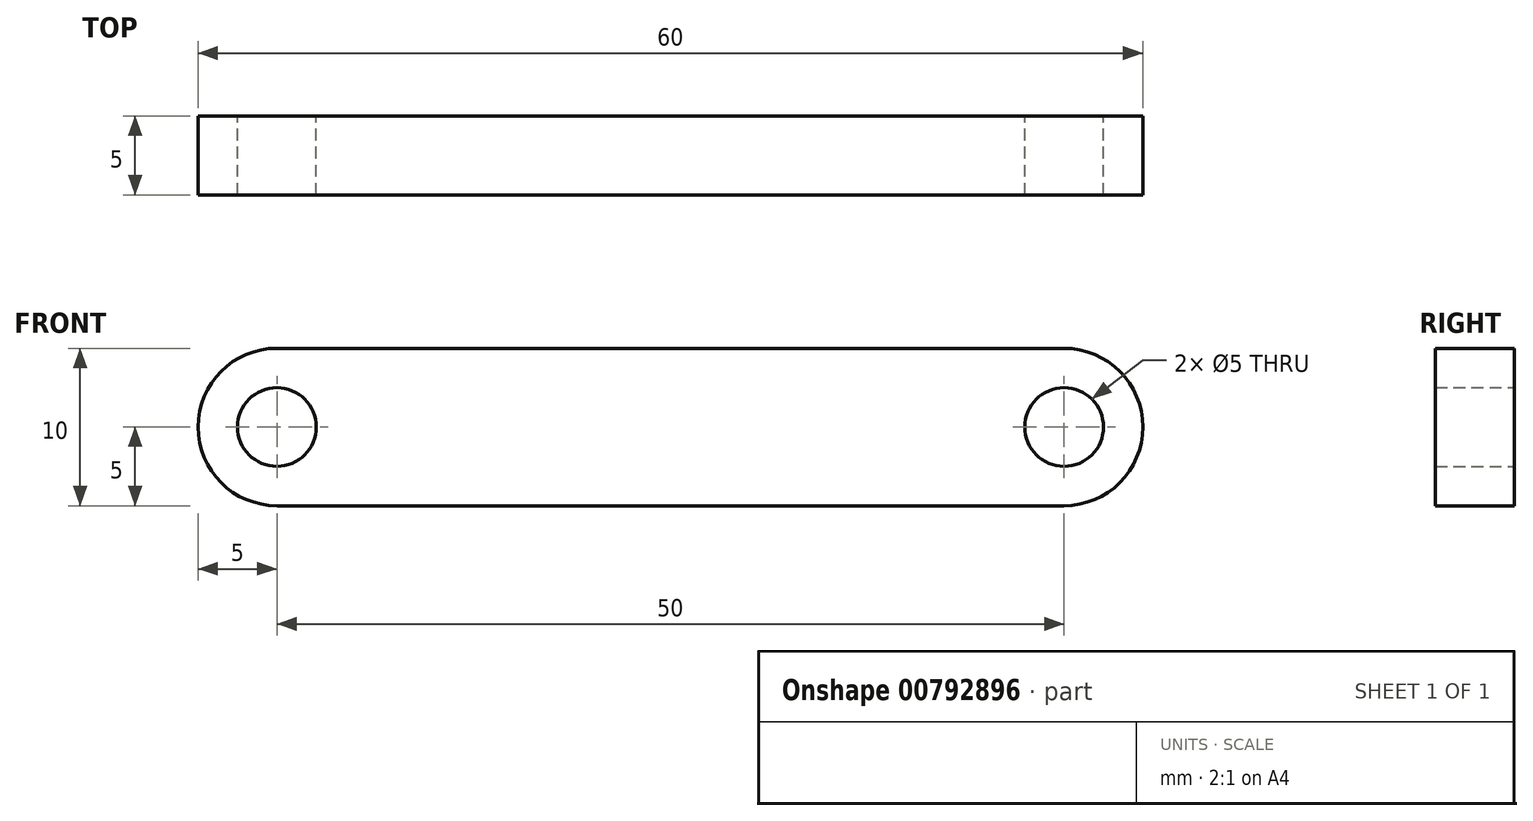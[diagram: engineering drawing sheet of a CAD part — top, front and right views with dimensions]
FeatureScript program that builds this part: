
annotation { "Feature Type Name" : "Feature", "Feature Type Description" : "" }
export const myFeature = defineFeature(function(context is Context, id is Id, definition is map)
    precondition{}
    {
        {
            var Q0;
            Q0=qCreatedBy(makeId("Front.planeOp"),FACE);
            var sketch = newSketch(context, id + "F0", { "sketchPlane" : qUnion([Q0])});
            skCircle(sketch, "E0", {"center": v(0, 0) * mm, "radius": 2.5 * mm});
            skArc(sketch, "E1", {"start": v(0, 5) * mm, "mid": v(-5, 0) * mm, "end": v(0, -5) * mm});
            skCircle(sketch, "E2", {"center": v(50, 0) * mm, "radius": 2.5 * mm});
            skArc(sketch, "E3", {"start": v(50, -5) * mm, "mid": v(55, 0) * mm, "end": v(50, 5) * mm});
            skLineSegment(sketch, "E4", {"start": v(50, -5) * mm, "end": v(0, -5) * mm});
            skLineSegment(sketch, "E5", {"start": v(0, 5) * mm, "end": v(50, 5) * mm});
            skSolve(sketch);
        }
        {
            var Q0;
            Q0=makeQuery(id+"F0.imprint","IMPRINT",FACE,{"disambiguationData":[TD([[makeQuery(id+"F0.imprint","IMPRINT",EDGE,{"derivedFrom":sQuery(id+"F0.wireOp",EDGE,"E0")}),-1.0]])]});
            extrude(context, id + "F1", {"entities" : qUnion([Q0]), "depth" : 5 * mm, "offsetDistance" : 25 * mm});
        }
    });
